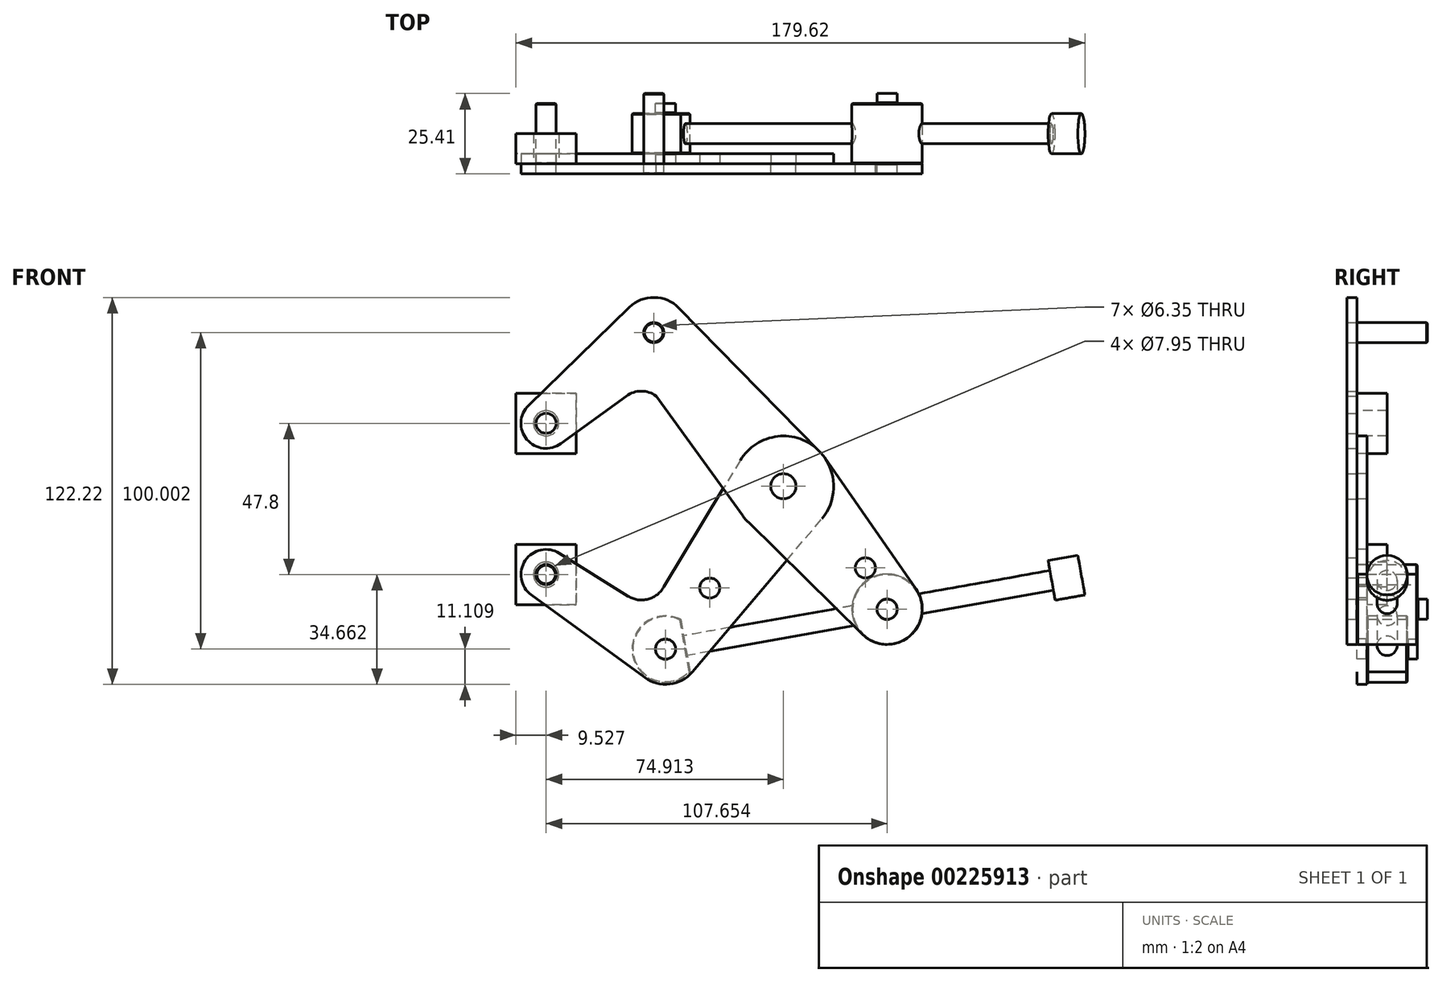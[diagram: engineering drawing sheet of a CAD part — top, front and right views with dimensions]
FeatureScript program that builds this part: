
annotation { "Feature Type Name" : "Feature", "Feature Type Description" : "" }
export const myFeature = defineFeature(function(context is Context, id is Id, definition is map)
    precondition{}
    {
        {
            var Q0;
            Q0=qCreatedBy(makeId("Front.planeOp"),FACE);
            var sketch = newSketch(context, id + "F0", { "sketchPlane" : qUnion([Q0])});
            skCircle(sketch, "E0", {"center": v(0, 0) * mm, "radius": 15.88 * mm});
            skCircle(sketch, "E1", {"center": v(0, 0) * mm, "radius": 3.98 * mm});
            skCircle(sketch, "E2", {"center": v(-40.93, 48.55) * mm, "radius": 11.11 * mm});
            skCircle(sketch, "E3", {"center": v(32.74, -38.84) * mm, "radius": 11.11 * mm});
            skLineSegment(sketch, "E4", {"start": v(-40.93, 48.55) * mm, "end": v(32.74, -38.84) * mm, "construction": true});
            skCircle(sketch, "E5", {"center": v(-74.91, 19.9) * mm, "radius": 7.94 * mm});
            skLineSegment(sketch, "E6", {"start": v(-40.93, 48.55) * mm, "end": v(-74.91, 19.9) * mm, "construction": true});
            skCircle(sketch, "E7", {"center": v(-74.91, 19.9) * mm, "radius": 3.18 * mm});
            skCircle(sketch, "E8", {"center": v(32.74, -38.84) * mm, "radius": 3.18 * mm});
            skCircle(sketch, "E9", {"center": v(25.88, -25.77) * mm, "radius": 3.18 * mm});
            skLineSegment(sketch, "E10", {"start": v(41.87, -32.5) * mm, "end": v(13.04, 9.05) * mm});
            skLineSegment(sketch, "E11", {"start": v(11.34, 11.11) * mm, "end": v(-33, 56.33) * mm});
            skLineSegment(sketch, "E12", {"start": v(-48.68, 56.51) * mm, "end": v(-80.45, 25.6) * mm});
            skLineSegment(sketch, "E13", {"start": v(-70.24, 13.48) * mm, "end": v(-49.54, 28.54) * mm});
            skArc(sketch, "E14", {"start": v(-40.19, 28.54) * mm, "mid": v(-44.86, 30.06) * mm, "end": v(-49.54, 28.54) * mm});
            skLineSegment(sketch, "E15", {"start": v(-40.19, 28.54) * mm, "end": v(-12.87, -9.3) * mm});
            skLineSegment(sketch, "E16", {"start": v(-11.13, -11.32) * mm, "end": v(24.95, -46.77) * mm});
            skLineSegment(sketch, "E17", {"start": v(0, 0) * mm, "end": v(-37.22, -51.45) * mm, "construction": true});
            skCircle(sketch, "E18", {"center": v(-37.22, -51.45) * mm, "radius": 11.11 * mm});
            skCircle(sketch, "E19", {"center": v(-37.22, -51.45) * mm, "radius": 3.18 * mm});
            skLineSegment(sketch, "E20", {"start": v(-37.22, -51.45) * mm, "end": v(-74.91, -27.9) * mm, "construction": true});
            skCircle(sketch, "E21", {"center": v(-74.91, -27.9) * mm, "radius": 7.94 * mm});
            skCircle(sketch, "E22", {"center": v(-74.91, -27.9) * mm, "radius": 3.18 * mm});
            skCircle(sketch, "E23", {"center": v(-23.25, -32.15) * mm, "radius": 3.18 * mm});
            skLineSegment(sketch, "E24", {"start": v(-74.91, 19.9) * mm, "end": v(-74.91, -27.9) * mm, "construction": true});
            skLineSegment(sketch, "E25", {"start": v(-79.59, -34.31) * mm, "end": v(-43.76, -60.43) * mm});
            skLineSegment(sketch, "E26", {"start": v(-28.73, -58.62) * mm, "end": v(12.13, -10.24) * mm});
            skLineSegment(sketch, "E27", {"start": v(-70.7, -21.17) * mm, "end": v(-49, -34.73) * mm});
            skLineSegment(sketch, "E28", {"start": v(-13.58, 8.22) * mm, "end": v(-37.75, -31.7) * mm});
            skArc(sketch, "E29", {"start": v(-49, -34.73) * mm, "mid": v(-42.71, -35.66) * mm, "end": v(-37.75, -31.7) * mm});
            skCircle(sketch, "E30", {"center": v(-40.93, 48.55) * mm, "radius": 3.18 * mm});
            skSolve(sketch);
        }
        {
            var Q0;
            {var subQ8=sQuery(id+"F0.wireOp",EDGE,"E11");Q0=makeQuery(id+"F0.imprint","IMPRINT",FACE,{"disambiguationData":[TD([[makeQuery(id+"F0.imprint","IMPRINT",EDGE,{"derivedFrom":subQ8}),1.0]])]});}
            var Q1;
            Q1=makeQuery(id+"F0.imprint","IMPRINT",FACE,{"disambiguationData":[TD([[makeQuery(id+"F0.imprint","IMPRINT",EDGE,{"derivedFrom":sQuery(id+"F0.wireOp",EDGE,"E30")}),-1.0]])]});
            var Q2;
            Q2=makeQuery(id+"F0.imprint","IMPRINT",FACE,{"disambiguationData":[TD([[makeQuery(id+"F0.imprint","IMPRINT",EDGE,{"derivedFrom":sQuery(id+"F0.wireOp",EDGE,"E7")}),-1.0]])]});
            var Q3;
            {var subQ0=sQuery(id+"F0.wireOp",EDGE,"E16");var subQ1=sQuery(id+"F0.wireOp",EDGE,"E0");var subQ2=makeQuery(id+"F0.imprint","INTERSECT",VERTEX,{"derivedFrom":[subQ1,subQ0]});Q3=makeQuery(id+"F0.imprint","IMPRINT",FACE,{"disambiguationData":[TD([[makeQuery(id+"F0.imprint","IMPRINT",EDGE,{"disambiguationData":[TD([[subQ2,-1.0]])],"derivedFrom":subQ1}),-1.0]])]});}
            var Q4;
            {var subQ0=sQuery(id+"F0.wireOp",EDGE,"E15");var subQ1=sQuery(id+"F0.wireOp",EDGE,"E0");var subQ2=makeQuery(id+"F0.imprint","INTERSECT",VERTEX,{"derivedFrom":[subQ1,subQ0]});Q4=makeQuery(id+"F0.imprint","IMPRINT",FACE,{"disambiguationData":[TD([[makeQuery(id+"F0.imprint","IMPRINT",EDGE,{"disambiguationData":[TD([[subQ2,1.0]])],"derivedFrom":subQ1}),-1.0]])]});}
            var Q5;
            Q5=makeQuery(id+"F0.imprint","IMPRINT",FACE,{"disambiguationData":[TD([[makeQuery(id+"F0.imprint","IMPRINT",EDGE,{"derivedFrom":sQuery(id+"F0.wireOp",EDGE,"E1")}),-1.0]])]});
            var Q6;
            Q6=makeQuery(id+"F0.imprint","IMPRINT",FACE,{"disambiguationData":[TD([[makeQuery(id+"F0.imprint","IMPRINT",EDGE,{"derivedFrom":sQuery(id+"F0.wireOp",EDGE,"E9")}),-1.0]])]});
            var Q7;
            Q7=makeQuery(id+"F0.imprint","IMPRINT",FACE,{"disambiguationData":[TD([[makeQuery(id+"F0.imprint","IMPRINT",EDGE,{"derivedFrom":sQuery(id+"F0.wireOp",EDGE,"E8")}),-1.0]])]});
            extrude(context, id + "F1", {"entities" : qUnion([Q0, Q1, Q2, Q3, Q4, Q5, Q6, Q7]), "depth" : 3.17 * mm});
        }
        {
            var Q0;
            Q0=makeQuery(id+"F0.imprint","IMPRINT",FACE,{"disambiguationData":[TD([[makeQuery(id+"F0.imprint","IMPRINT",EDGE,{"derivedFrom":sQuery(id+"F0.wireOp",EDGE,"E23")}),-1.0]])]});
            var Q1;
            {var subQ0=sQuery(id+"F0.wireOp",EDGE,"E15");var subQ1=sQuery(id+"F0.wireOp",EDGE,"E0");var subQ2=makeQuery(id+"F0.imprint","INTERSECT",VERTEX,{"derivedFrom":[subQ1,subQ0]});Q1=makeQuery(id+"F0.imprint","IMPRINT",FACE,{"disambiguationData":[TD([[makeQuery(id+"F0.imprint","IMPRINT",EDGE,{"disambiguationData":[TD([[subQ2,1.0]])],"derivedFrom":subQ1}),-1.0]])]});}
            var Q2;
            {var subQ0=sQuery(id+"F0.wireOp",EDGE,"E16");var subQ1=sQuery(id+"F0.wireOp",EDGE,"E0");var subQ2=makeQuery(id+"F0.imprint","INTERSECT",VERTEX,{"derivedFrom":[subQ1,subQ0]});Q2=makeQuery(id+"F0.imprint","IMPRINT",FACE,{"disambiguationData":[TD([[makeQuery(id+"F0.imprint","IMPRINT",EDGE,{"disambiguationData":[TD([[subQ2,-1.0]])],"derivedFrom":subQ1}),-1.0]])]});}
            var Q3;
            Q3=makeQuery(id+"F0.imprint","IMPRINT",FACE,{"disambiguationData":[TD([[makeQuery(id+"F0.imprint","IMPRINT",EDGE,{"derivedFrom":sQuery(id+"F0.wireOp",EDGE,"E1")}),-1.0]])]});
            var Q4;
            Q4=makeQuery(id+"F0.imprint","IMPRINT",FACE,{"disambiguationData":[TD([[makeQuery(id+"F0.imprint","IMPRINT",EDGE,{"derivedFrom":sQuery(id+"F0.wireOp",EDGE,"E19")}),-1.0]])]});
            var Q5;
            Q5=makeQuery(id+"F0.imprint","IMPRINT",FACE,{"disambiguationData":[TD([[makeQuery(id+"F0.imprint","IMPRINT",EDGE,{"derivedFrom":sQuery(id+"F0.wireOp",EDGE,"E22")}),-1.0]])]});
            extrude(context, id + "F2", {"entities" : qUnion([Q0, Q1, Q2, Q3, Q4, Q5]), "oppositeDirection" : true, "depth" : 3.17 * mm});
        }
        {
            var Q0;
            Q0=makeQuery(id+"F1.opExtrude","CAP_FACE",FACE,{"disambiguationData":[OSD([sQuery(id+"F0.wireOp",EDGE,"E0"),sQuery(id+"F0.wireOp",EDGE,"E1"),sQuery(id+"F0.wireOp",EDGE,"E2"),sQuery(id+"F0.wireOp",EDGE,"E3"),sQuery(id+"F0.wireOp",EDGE,"E5"),sQuery(id+"F0.wireOp",EDGE,"E7"),sQuery(id+"F0.wireOp",EDGE,"E8"),sQuery(id+"F0.wireOp",EDGE,"E9"),sQuery(id+"F0.wireOp",EDGE,"E10"),sQuery(id+"F0.wireOp",EDGE,"E11"),sQuery(id+"F0.wireOp",EDGE,"E12"),sQuery(id+"F0.wireOp",EDGE,"E13"),sQuery(id+"F0.wireOp",EDGE,"E14"),sQuery(id+"F0.wireOp",EDGE,"E15"),sQuery(id+"F0.wireOp",EDGE,"E16"),sQuery(id+"F0.wireOp",EDGE,"E30")])],"isStart":false});
            var sketch = newSketch(context, id + "F3", { "sketchPlane" : qUnion([Q0])});
            skCircle(sketch, "E31", {"center": v(-40.93, 48.55) * mm, "radius": 3.98 * mm});
            skCircle(sketch, "E32", {"center": v(0, 0) * mm, "radius": 3.98 * mm});
            skCircle(sketch, "E33", {"center": v(32.74, -38.84) * mm, "radius": 11.11 * mm});
            skSolve(sketch);
        }
        {
            var Q0;
            Q0=makeQuery(id+"F2.opExtrude","CAP_FACE",FACE,{"disambiguationData":[OSD([sQuery(id+"F0.wireOp",EDGE,"E0"),sQuery(id+"F0.wireOp",EDGE,"E1"),sQuery(id+"F0.wireOp",EDGE,"E18"),sQuery(id+"F0.wireOp",EDGE,"E19"),sQuery(id+"F0.wireOp",EDGE,"E21"),sQuery(id+"F0.wireOp",EDGE,"E22"),sQuery(id+"F0.wireOp",EDGE,"E23"),sQuery(id+"F0.wireOp",EDGE,"E25"),sQuery(id+"F0.wireOp",EDGE,"E26"),sQuery(id+"F0.wireOp",EDGE,"E27"),sQuery(id+"F0.wireOp",EDGE,"E28"),sQuery(id+"F0.wireOp",EDGE,"E29")])],"isStart":true});
            var sketch = newSketch(context, id + "F4", { "sketchPlane" : qUnion([Q0])});
            skCircle(sketch, "E34", {"center": v(-37.22, -51.45) * mm, "radius": 10.54 * mm});
            skCircle(sketch, "E35", {"center": v(-74.91, -27.9) * mm, "radius": 3.98 * mm});
            skLineSegment(sketch, "E36", {"start": v(32.84, -39.22) * mm, "end": v(-37.22, -51.45) * mm, "construction": true});
            skLineSegment(sketch, "E37", {"start": v(-32.44, -42.05) * mm, "end": v(-29.49, -58.62) * mm});
            skSolve(sketch);
        }
        {
            var Q0;
            Q0=qCreatedBy(makeId("Front.planeOp"),FACE);
            cPlane(context, id + "F5", {"entities" : qUnion([Q0]), "cplaneType" : CPlaneType.OFFSET, "offset" : 9.52 * mm, "oppositeDirection" : true, "width" : 152.4 * mm, "height" : 152.4 * mm});
        }
        {
            var Q0;
            Q0=makeQuery(id+"F4.imprint","IMPRINT",FACE,{"disambiguationData":[TD([[makeQuery(id+"F4.imprint","IMPRINT",EDGE,{"derivedFrom":makeQuery(id+"F2.opExtrude","CAP_EDGE",EDGE,{"disambiguationData":[OSD([sQuery(id+"F0.wireOp",EDGE,"E22")])],"isStart":true})}),1.0]])]});
            var Q1;
            Q1=makeQuery(id+"F4.imprint","IMPRINT",FACE,{"disambiguationData":[TD([[makeQuery(id+"F4.imprint","IMPRINT",EDGE,{"derivedFrom":makeQuery(id+"F2.opExtrude","CAP_EDGE",EDGE,{"disambiguationData":[OSD([sQuery(id+"F0.wireOp",EDGE,"E19")])],"isStart":true})}),1.0]])]});
            var Q2;
            Q2=makeQuery(id+"F4.imprint","IMPRINT",FACE,{"disambiguationData":[TD([[makeQuery(id+"F4.imprint","IMPRINT",EDGE,{"derivedFrom":makeQuery(id+"F2.opExtrude","CAP_EDGE",EDGE,{"disambiguationData":[OSD([sQuery(id+"F0.wireOp",EDGE,"E19")])],"isStart":true})}),-1.0]])]});
            var Q3;
            Q3=makeQuery(id+"F3.imprint","IMPRINT",FACE,{"disambiguationData":[TD([[makeQuery(id+"F3.imprint","IMPRINT",EDGE,{"derivedFrom":makeQuery(id+"F1.opExtrude","CAP_EDGE",EDGE,{"disambiguationData":[OSD([sQuery(id+"F0.wireOp",EDGE,"E8")])],"isStart":false})}),1.0]])]});
            var Q4;
            Q4=makeQuery(id+"F3.imprint","IMPRINT",FACE,{"disambiguationData":[TD([[makeQuery(id+"F3.imprint","IMPRINT",EDGE,{"derivedFrom":makeQuery(id+"F1.opExtrude","CAP_EDGE",EDGE,{"disambiguationData":[OSD([sQuery(id+"F0.wireOp",EDGE,"E30")])],"isStart":false})}),1.0]])]});
            var Q5;
            Q5=makeQuery(id+"F3.imprint","IMPRINT",FACE,{"disambiguationData":[TD([[makeQuery(id+"F3.imprint","IMPRINT",EDGE,{"derivedFrom":makeQuery(id+"F1.opExtrude","CAP_EDGE",EDGE,{"disambiguationData":[OSD([sQuery(id+"F0.wireOp",EDGE,"E8")])],"isStart":false})}),-1.0]])]});
            var Q6;
            Q6=qCreatedBy(id+"F5.planeOp",FACE);
            extrude(context, id + "F6", {"entities" : qUnion([Q0, Q1, Q2, Q3, Q4, Q5]), "endBound" : BoundingType.UP_TO_SURFACE, "oppositeDirection" : true, "endBoundEntityFace" : qUnion([Q6]), "depth" : 25.4 * mm});
        }
        {
            var Q0;
            Q0=makeQuery(id+"F1.opExtrude","SWEPT_BODY",BODY,{"disambiguationData":[OSD([sQuery(id+"F0.wireOp",EDGE,"E0"),sQuery(id+"F0.wireOp",EDGE,"E1"),sQuery(id+"F0.wireOp",EDGE,"E2"),sQuery(id+"F0.wireOp",EDGE,"E3"),sQuery(id+"F0.wireOp",EDGE,"E5"),sQuery(id+"F0.wireOp",EDGE,"E7"),sQuery(id+"F0.wireOp",EDGE,"E8"),sQuery(id+"F0.wireOp",EDGE,"E9"),sQuery(id+"F0.wireOp",EDGE,"E10"),sQuery(id+"F0.wireOp",EDGE,"E11"),sQuery(id+"F0.wireOp",EDGE,"E12"),sQuery(id+"F0.wireOp",EDGE,"E13"),sQuery(id+"F0.wireOp",EDGE,"E14"),sQuery(id+"F0.wireOp",EDGE,"E15"),sQuery(id+"F0.wireOp",EDGE,"E16"),sQuery(id+"F0.wireOp",EDGE,"E30")])]});
            var Q1;
            Q1=makeQuery(id+"F2.opExtrude","SWEPT_BODY",BODY,{"disambiguationData":[OSD([sQuery(id+"F0.wireOp",EDGE,"E0"),sQuery(id+"F0.wireOp",EDGE,"E1"),sQuery(id+"F0.wireOp",EDGE,"E18"),sQuery(id+"F0.wireOp",EDGE,"E19"),sQuery(id+"F0.wireOp",EDGE,"E21"),sQuery(id+"F0.wireOp",EDGE,"E22"),sQuery(id+"F0.wireOp",EDGE,"E23"),sQuery(id+"F0.wireOp",EDGE,"E25"),sQuery(id+"F0.wireOp",EDGE,"E26"),sQuery(id+"F0.wireOp",EDGE,"E27"),sQuery(id+"F0.wireOp",EDGE,"E28"),sQuery(id+"F0.wireOp",EDGE,"E29")])]});
            var Q2;
            Q2=makeQuery(id+"F6.opExtrude","SWEPT_BODY",BODY,{"disambiguationData":[OSD([sQuery(id+"F0.wireOp",EDGE,"E30")])]});
            var Q3;
            Q3=makeQuery(id+"F6.opExtrude","SWEPT_BODY",BODY,{"disambiguationData":[OSD([sQuery(id+"F3.wireOp",EDGE,"E33")])]});
            var Q4;
            Q4=makeQuery(id+"F6.opExtrude","SWEPT_BODY",BODY,{"disambiguationData":[OSD([sQuery(id+"F0.wireOp",EDGE,"E18"),sQuery(id+"F0.wireOp",EDGE,"E25"),sQuery(id+"F4.wireOp",EDGE,"E34"),sQuery(id+"F4.wireOp",EDGE,"8R5mYEVv-fxpU-NJea-VH3M-GI5tbgevVIEk")])]});
            var Q5;
            Q5=makeQuery(id+"F6.opExtrude","SWEPT_BODY",BODY,{"disambiguationData":[OSD([sQuery(id+"F0.wireOp",EDGE,"E22")])]});
            booleanBodies(context, id + "F7", {"operationType" : BooleanOperationType.SUBTRACTION, "tools" : qUnion([Q0, Q1]), "targets" : qUnion([Q2, Q3, Q4, Q5]), "keepTools" : true});
        }
        {
            var Q0;
            Q0=makeQuery(id+"F6.opExtrude","CAP_EDGE",EDGE,{"disambiguationData":[OSD([sQuery(id+"F0.wireOp",EDGE,"E30")])],"isStart":true});
            var Q1;
            Q1=makeQuery(id+"F6.opExtrude","CAP_EDGE",EDGE,{"disambiguationData":[OSD([sQuery(id+"F0.wireOp",EDGE,"E22")])],"isStart":true});
            var Q2;
            Q2=makeQuery(id+"F7.opBoolean","COPY",EDGE,{"derivedFrom":makeQuery(id+"F1.opExtrude","CAP_EDGE",EDGE,{"disambiguationData":[OSD([sQuery(id+"F0.wireOp",EDGE,"E8")])],"isStart":false})});
            var Q3;
            Q3=makeQuery(id+"F7.opBoolean","COPY",EDGE,{"derivedFrom":makeQuery(id+"F2.opExtrude","CAP_EDGE",EDGE,{"disambiguationData":[OSD([sQuery(id+"F0.wireOp",EDGE,"E19")])],"isStart":true})});
            var Q4;
            Q4=makeQuery(id+"F7.opBoolean","INTERSECT",EDGE,{"derivedFrom":[makeQuery(id+"F2.opExtrude","CAP_FACE",FACE,{"disambiguationData":[OSD([sQuery(id+"F0.wireOp",EDGE,"E0"),sQuery(id+"F0.wireOp",EDGE,"E1"),sQuery(id+"F0.wireOp",EDGE,"E18"),sQuery(id+"F0.wireOp",EDGE,"E19"),sQuery(id+"F0.wireOp",EDGE,"E21"),sQuery(id+"F0.wireOp",EDGE,"E22"),sQuery(id+"F0.wireOp",EDGE,"E23"),sQuery(id+"F0.wireOp",EDGE,"E25"),sQuery(id+"F0.wireOp",EDGE,"E26"),sQuery(id+"F0.wireOp",EDGE,"E27"),sQuery(id+"F0.wireOp",EDGE,"E28"),sQuery(id+"F0.wireOp",EDGE,"E29")])],"isStart":false}),makeQuery(id+"F6.opExtrude","SWEPT_FACE",FACE,{"disambiguationData":[OSD([sQuery(id+"F4.wireOp",EDGE,"E34")])]})]});
            var Q5;
            Q5=makeQuery(id+"F7.opBoolean","COPY",FACE,{"derivedFrom":makeQuery(id+"F2.opExtrude","CAP_FACE",FACE,{"disambiguationData":[OSD([sQuery(id+"F0.wireOp",EDGE,"E0"),sQuery(id+"F0.wireOp",EDGE,"E1"),sQuery(id+"F0.wireOp",EDGE,"E18"),sQuery(id+"F0.wireOp",EDGE,"E19"),sQuery(id+"F0.wireOp",EDGE,"E21"),sQuery(id+"F0.wireOp",EDGE,"E22"),sQuery(id+"F0.wireOp",EDGE,"E23"),sQuery(id+"F0.wireOp",EDGE,"E25"),sQuery(id+"F0.wireOp",EDGE,"E26"),sQuery(id+"F0.wireOp",EDGE,"E27"),sQuery(id+"F0.wireOp",EDGE,"E28"),sQuery(id+"F0.wireOp",EDGE,"E29")])],"isStart":false})});
            var Q6;
            Q6=makeQuery(id+"F7.opBoolean","COPY",FACE,{"derivedFrom":makeQuery(id+"F1.opExtrude","CAP_FACE",FACE,{"disambiguationData":[OSD([sQuery(id+"F0.wireOp",EDGE,"E0"),sQuery(id+"F0.wireOp",EDGE,"E1"),sQuery(id+"F0.wireOp",EDGE,"E2"),sQuery(id+"F0.wireOp",EDGE,"E3"),sQuery(id+"F0.wireOp",EDGE,"E5"),sQuery(id+"F0.wireOp",EDGE,"E7"),sQuery(id+"F0.wireOp",EDGE,"E8"),sQuery(id+"F0.wireOp",EDGE,"E9"),sQuery(id+"F0.wireOp",EDGE,"E10"),sQuery(id+"F0.wireOp",EDGE,"E11"),sQuery(id+"F0.wireOp",EDGE,"E12"),sQuery(id+"F0.wireOp",EDGE,"E13"),sQuery(id+"F0.wireOp",EDGE,"E14"),sQuery(id+"F0.wireOp",EDGE,"E15"),sQuery(id+"F0.wireOp",EDGE,"E16"),sQuery(id+"F0.wireOp",EDGE,"E30")])],"isStart":true})});
            chamfer(context, id + "F8", {"entities" : qUnion([Q0, Q1, Q2, Q3, Q4, Q5, Q6]), "width" : 0.25 * mm, "tangentPropagation" : true});
        }
        {
            var Q0;
            Q0=makeQuery(id+"F6.opExtrude","SWEPT_BODY",BODY,{"disambiguationData":[OSD([sQuery(id+"F0.wireOp",EDGE,"E30")])]});
            var Q1;
            Q1=makeQuery(id+"F6.opExtrude","SWEPT_BODY",BODY,{"disambiguationData":[OSD([sQuery(id+"F0.wireOp",EDGE,"E22")])]});
            var Q2;
            Q2=makeQuery(id+"F6.opExtrude","SWEPT_BODY",BODY,{"disambiguationData":[OSD([sQuery(id+"F0.wireOp",EDGE,"E18"),sQuery(id+"F0.wireOp",EDGE,"E25"),sQuery(id+"F4.wireOp",EDGE,"E34"),sQuery(id+"F4.wireOp",EDGE,"8R5mYEVv-fxpU-NJea-VH3M-GI5tbgevVIEk")])]});
            var Q3;
            Q3=makeQuery(id+"F6.opExtrude","SWEPT_BODY",BODY,{"disambiguationData":[OSD([sQuery(id+"F3.wireOp",EDGE,"E33")])]});
            var Q4;
            Q4=qCreatedBy(id+"F5.planeOp",FACE);
            mirror(context, id + "F9", {"entities" : qUnion([Q0, Q1, Q2, Q3]), "mirrorPlane" : qUnion([Q4])});
        }
        {
            var Q0;
            Q0=makeQuery(id+"F9.opPattern","COPY",BODY,{"derivedFrom":makeQuery(id+"F6.opExtrude","SWEPT_BODY",BODY,{"disambiguationData":[OSD([sQuery(id+"F0.wireOp",EDGE,"E30")])]}),"instanceName":"1"});
            var Q1;
            Q1=makeQuery(id+"F6.opExtrude","SWEPT_BODY",BODY,{"disambiguationData":[OSD([sQuery(id+"F0.wireOp",EDGE,"E30")])]});
            var Q2;
            Q2=makeQuery(id+"F9.opPattern","COPY",BODY,{"derivedFrom":makeQuery(id+"F6.opExtrude","SWEPT_BODY",BODY,{"disambiguationData":[OSD([sQuery(id+"F0.wireOp",EDGE,"E22")])]}),"instanceName":"1"});
            var Q3;
            Q3=makeQuery(id+"F6.opExtrude","SWEPT_BODY",BODY,{"disambiguationData":[OSD([sQuery(id+"F0.wireOp",EDGE,"E22")])]});
            var Q4;
            Q4=makeQuery(id+"F9.opPattern","COPY",BODY,{"derivedFrom":makeQuery(id+"F6.opExtrude","SWEPT_BODY",BODY,{"disambiguationData":[OSD([sQuery(id+"F3.wireOp",EDGE,"E33")])]}),"instanceName":"1"});
            var Q5;
            Q5=makeQuery(id+"F6.opExtrude","SWEPT_BODY",BODY,{"disambiguationData":[OSD([sQuery(id+"F3.wireOp",EDGE,"E33")])]});
            var Q6;
            Q6=makeQuery(id+"F9.opPattern","COPY",BODY,{"derivedFrom":makeQuery(id+"F6.opExtrude","SWEPT_BODY",BODY,{"disambiguationData":[OSD([sQuery(id+"F0.wireOp",EDGE,"E18"),sQuery(id+"F0.wireOp",EDGE,"E25"),sQuery(id+"F4.wireOp",EDGE,"E34"),sQuery(id+"F4.wireOp",EDGE,"8R5mYEVv-fxpU-NJea-VH3M-GI5tbgevVIEk")])]}),"instanceName":"1"});
            var Q7;
            Q7=makeQuery(id+"F6.opExtrude","SWEPT_BODY",BODY,{"disambiguationData":[OSD([sQuery(id+"F0.wireOp",EDGE,"E18"),sQuery(id+"F0.wireOp",EDGE,"E25"),sQuery(id+"F4.wireOp",EDGE,"E34"),sQuery(id+"F4.wireOp",EDGE,"8R5mYEVv-fxpU-NJea-VH3M-GI5tbgevVIEk")])]});
            booleanBodies(context, id + "F10", {"operationType" : BooleanOperationType.UNION, "tools" : qUnion([Q0, Q1, Q2, Q3, Q4, Q5, Q6, Q7])});
        }
        {
            var Q0;
            {var subQ0=makeQuery(id+"F6.opExtrude","SWEPT_FACE",FACE,{"disambiguationData":[OSD([sQuery(id+"F4.wireOp",EDGE,"E37")])]});Q0=makeQuery(id+"F10.opBoolean","MERGE",FACE,{"derivedFrom":[subQ0,makeQuery(id+"F9.opPattern","COPY",FACE,{"derivedFrom":subQ0,"instanceName":"1"})]});}
            var sketch = newSketch(context, id + "F11", { "sketchPlane" : qUnion([Q0])});
            skLineSegment(sketch, "E38.0.0", {"start": v(15.62, -35.71) * mm, "end": v(3.43, -35.71) * mm});
            skLineSegment(sketch, "E38.0.1", {"start": v(3.43, -35.71) * mm, "end": v(3.43, -52.54) * mm});
            skLineSegment(sketch, "E39", {"start": v(9.52, -35.71) * mm, "end": v(9.52, -52.54) * mm, "construction": true});
            skCircle(sketch, "E40", {"center": v(9.52, -44.13) * mm, "radius": 3.18 * mm});
            skSolve(sketch);
        }
        {
            var Q0;
            Q0 = qSketchRegion(id + "F11", true);
            extrude(context, id + "F12", {"entities" : qUnion([Q0]), "operationType" : NewBodyOperationType.ADD, "oppositeDirection" : true, "depth" : 12.7 * mm});
        }
        {
            var Q0;
            Q0 = qSketchRegion(id + "F11", true);
            extrude(context, id + "F13", {"entities" : qUnion([Q0]), "operationType" : NewBodyOperationType.ADD, "depth" : 127 * mm});
        }
        {
            var Q0;
            Q0=makeQuery(id+"F13.opExtrude","CAP_FACE",FACE,{"disambiguationData":[OSD([sQuery(id+"F11.wireOp",EDGE,"E40")])],"isStart":false});
            var sketch = newSketch(context, id + "F14", { "sketchPlane" : qUnion([Q0])});
            skCircle(sketch, "E41.0", {"center": v(9.52, -44.13) * mm, "radius": 3.18 * mm});
            skCircle(sketch, "E42", {"center": v(9.52, -44.13) * mm, "radius": 6.35 * mm});
            skSolve(sketch);
        }
        {
            var Q0;
            Q0 = qSketchRegion(id + "F14", true);
            var Q1;
            Q1=makeQuery(id+"F14.imprint","IMPRINT",FACE,{"disambiguationData":[TD([[makeQuery(id+"F14.imprint","IMPRINT",EDGE,{"derivedFrom":sQuery(id+"F14.wireOp",EDGE,"E41.0")}),1.0]])]});
            extrude(context, id + "F15", {"entities" : qUnion([Q0, Q1]), "operationType" : NewBodyOperationType.ADD, "oppositeDirection" : true, "depth" : 9.52 * mm});
        }
        {
            var Q0;
            Q0=makeQuery(id+"F2.opExtrude","CAP_FACE",FACE,{"disambiguationData":[OSD([sQuery(id+"F0.wireOp",EDGE,"E0"),sQuery(id+"F0.wireOp",EDGE,"E1"),sQuery(id+"F0.wireOp",EDGE,"E18"),sQuery(id+"F0.wireOp",EDGE,"E19"),sQuery(id+"F0.wireOp",EDGE,"E21"),sQuery(id+"F0.wireOp",EDGE,"E22"),sQuery(id+"F0.wireOp",EDGE,"E23"),sQuery(id+"F0.wireOp",EDGE,"E25"),sQuery(id+"F0.wireOp",EDGE,"E26"),sQuery(id+"F0.wireOp",EDGE,"E27"),sQuery(id+"F0.wireOp",EDGE,"E28"),sQuery(id+"F0.wireOp",EDGE,"E29")])],"isStart":false});
            var sketch = newSketch(context, id + "F16", { "sketchPlane" : qUnion([Q0])});
            skCircle(sketch, "E43", {"center": v(74.91, -27.9) * mm, "radius": 3.98 * mm});
            skLineSegment(sketch, "E44.bottom", {"start": v(65.39, -18.37) * mm, "end": v(84.44, -18.37) * mm});
            skLineSegment(sketch, "E44.top", {"start": v(65.39, -37.42) * mm, "end": v(84.44, -37.42) * mm});
            skLineSegment(sketch, "E44.left", {"start": v(65.39, -18.37) * mm, "end": v(65.39, -37.42) * mm});
            skLineSegment(sketch, "E44.right", {"start": v(84.44, -18.37) * mm, "end": v(84.44, -37.42) * mm});
            skLineSegment(sketch, "E45", {"start": v(65.39, -18.37) * mm, "end": v(84.44, -37.42) * mm, "construction": true});
            skCircle(sketch, "E46", {"center": v(74.91, -27.9) * mm, "radius": 3.64 * mm, "construction": true});
            skSolve(sketch);
        }
        {
            var Q0;
            Q0=makeQuery(id+"F1.opExtrude","CAP_FACE",FACE,{"disambiguationData":[OSD([sQuery(id+"F0.wireOp",EDGE,"E0"),sQuery(id+"F0.wireOp",EDGE,"E1"),sQuery(id+"F0.wireOp",EDGE,"E2"),sQuery(id+"F0.wireOp",EDGE,"E3"),sQuery(id+"F0.wireOp",EDGE,"E5"),sQuery(id+"F0.wireOp",EDGE,"E7"),sQuery(id+"F0.wireOp",EDGE,"E8"),sQuery(id+"F0.wireOp",EDGE,"E9"),sQuery(id+"F0.wireOp",EDGE,"E10"),sQuery(id+"F0.wireOp",EDGE,"E11"),sQuery(id+"F0.wireOp",EDGE,"E12"),sQuery(id+"F0.wireOp",EDGE,"E13"),sQuery(id+"F0.wireOp",EDGE,"E14"),sQuery(id+"F0.wireOp",EDGE,"E15"),sQuery(id+"F0.wireOp",EDGE,"E16"),sQuery(id+"F0.wireOp",EDGE,"E30")])],"isStart":true});
            var sketch = newSketch(context, id + "F17", { "sketchPlane" : qUnion([Q0])});
            skCircle(sketch, "E47", {"center": v(74.91, 19.9) * mm, "radius": 3.98 * mm});
            skLineSegment(sketch, "E48.bottom", {"start": v(84.44, 29.43) * mm, "end": v(65.39, 29.43) * mm});
            skLineSegment(sketch, "E48.top", {"start": v(84.44, 10.38) * mm, "end": v(65.39, 10.38) * mm});
            skLineSegment(sketch, "E48.left", {"start": v(84.44, 29.43) * mm, "end": v(84.44, 10.38) * mm});
            skLineSegment(sketch, "E48.right", {"start": v(65.39, 29.43) * mm, "end": v(65.39, 10.38) * mm});
            skSolve(sketch);
        }
        {
            var Q0;
            {var subQ1=sQuery(id+"F17.wireOp",EDGE,"E48.top");Q0=makeQuery(id+"F17.imprint","IMPRINT",FACE,{"disambiguationData":[TD([[makeQuery(id+"F17.imprint","IMPRINT",EDGE,{"derivedFrom":subQ1}),-1.0]])]});}
            var Q1;
            Q1=makeQuery(id+"F17.imprint","IMPRINT",FACE,{"disambiguationData":[TD([[makeQuery(id+"F17.imprint","IMPRINT",EDGE,{"derivedFrom":sQuery(id+"F17.wireOp",EDGE,"E47")}),-1.0]])]});
            var Q2;
            {var subQ6=sQuery(id+"F16.wireOp",EDGE,"E44.bottom");Q2=makeQuery(id+"F16.imprint","IMPRINT",FACE,{"disambiguationData":[TD([[makeQuery(id+"F16.imprint","IMPRINT",EDGE,{"derivedFrom":subQ6}),-1.0]])]});}
            var Q3;
            Q3=makeQuery(id+"F16.imprint","IMPRINT",FACE,{"disambiguationData":[TD([[makeQuery(id+"F16.imprint","IMPRINT",EDGE,{"derivedFrom":sQuery(id+"F16.wireOp",EDGE,"E43")}),-1.0]])]});
            var Q4;
            Q4=qCreatedBy(id+"F5.planeOp",FACE);
            extrude(context, id + "F18", {"entities" : qUnion([Q0, Q1, Q2, Q3]), "endBound" : BoundingType.UP_TO_SURFACE, "endBoundEntityFace" : qUnion([Q4]), "depth" : 25.4 * mm});
        }
    });
